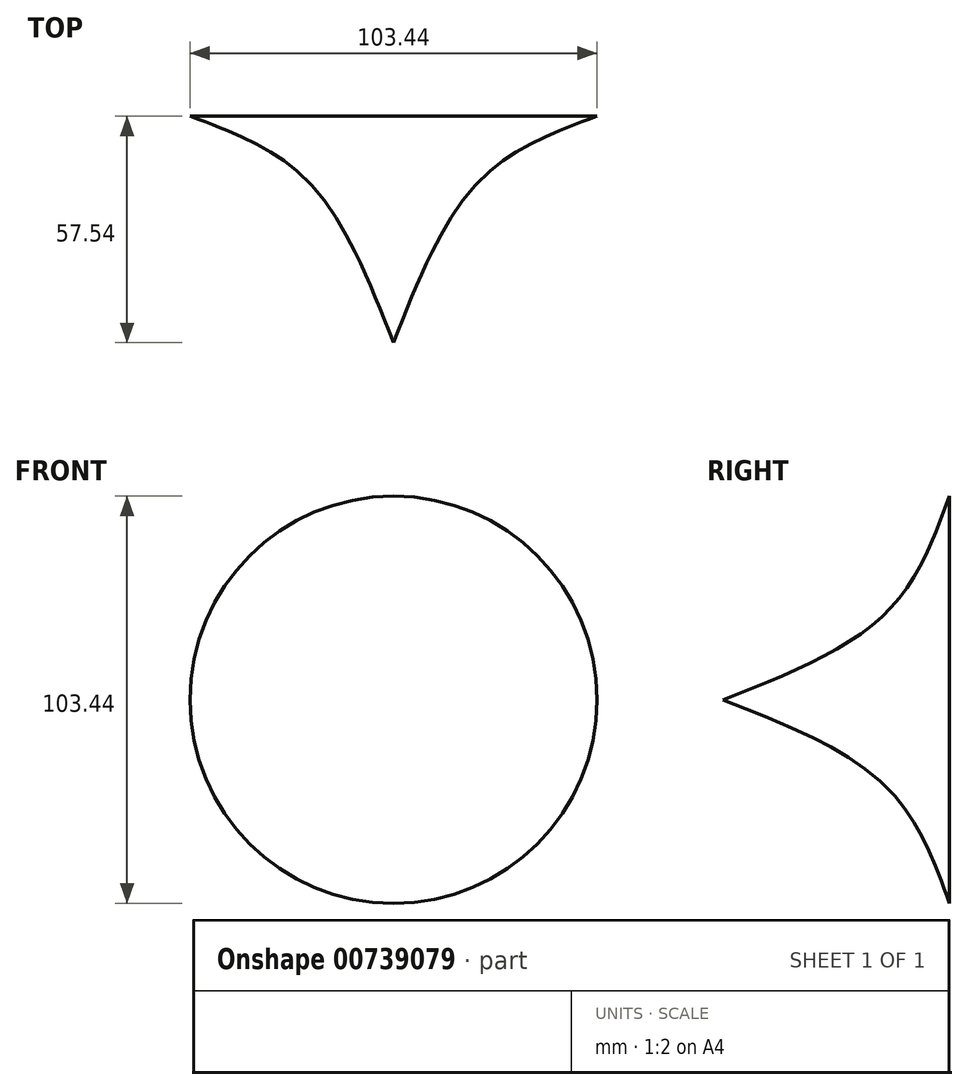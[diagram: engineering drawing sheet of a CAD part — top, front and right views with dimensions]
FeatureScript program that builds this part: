
annotation { "Feature Type Name" : "Feature", "Feature Type Description" : "" }
export const myFeature = defineFeature(function(context is Context, id is Id, definition is map)
    precondition{}
    {
        {
            var Q0;
            Q0=qCreatedBy(makeId("Right.planeOp"),FACE);
            var sketch = newSketch(context, id + "F0", { "sketchPlane" : qUnion([Q0])});
            skLineSegment(sketch, "E0", {"start": v(0, 0) * mm, "end": v(-57.54, 0) * mm});
            skFitSpline(sketch, "E1", {"points": [v(-57.54, 0) * mm, v(-16.14, 22.09) * mm, v(0, 51.72) * mm], "startDerivative": vector(87.68, 34.4) * mm, "endDerivative": vector(25.7, 70.03) * mm});
            skLineSegment(sketch, "E2", {"start": v(0, 51.72) * mm, "end": v(0, 0) * mm});
            skSolve(sketch);
        }
        {
            var Q0;
            Q0=makeQuery(id+"F0.imprint","IMPRINT",FACE,{"disambiguationData":[TD([[makeQuery(id+"F0.imprint","IMPRINT",EDGE,{"derivedFrom":sQuery(id+"F0.wireOp",EDGE,"E0")}),-1.0]])]});
            var Q1;
            Q1=sQuery(id+"F0.wireOp",EDGE,"E0");
            revolve(context, id + "F1", {"surfaceOperationType" : NewSurfaceOperationType.NEW, "entities" : qUnion([Q0]), "axis" : qUnion([Q1]), "revolveType" : RevolveType.FULL});
        }
    });
